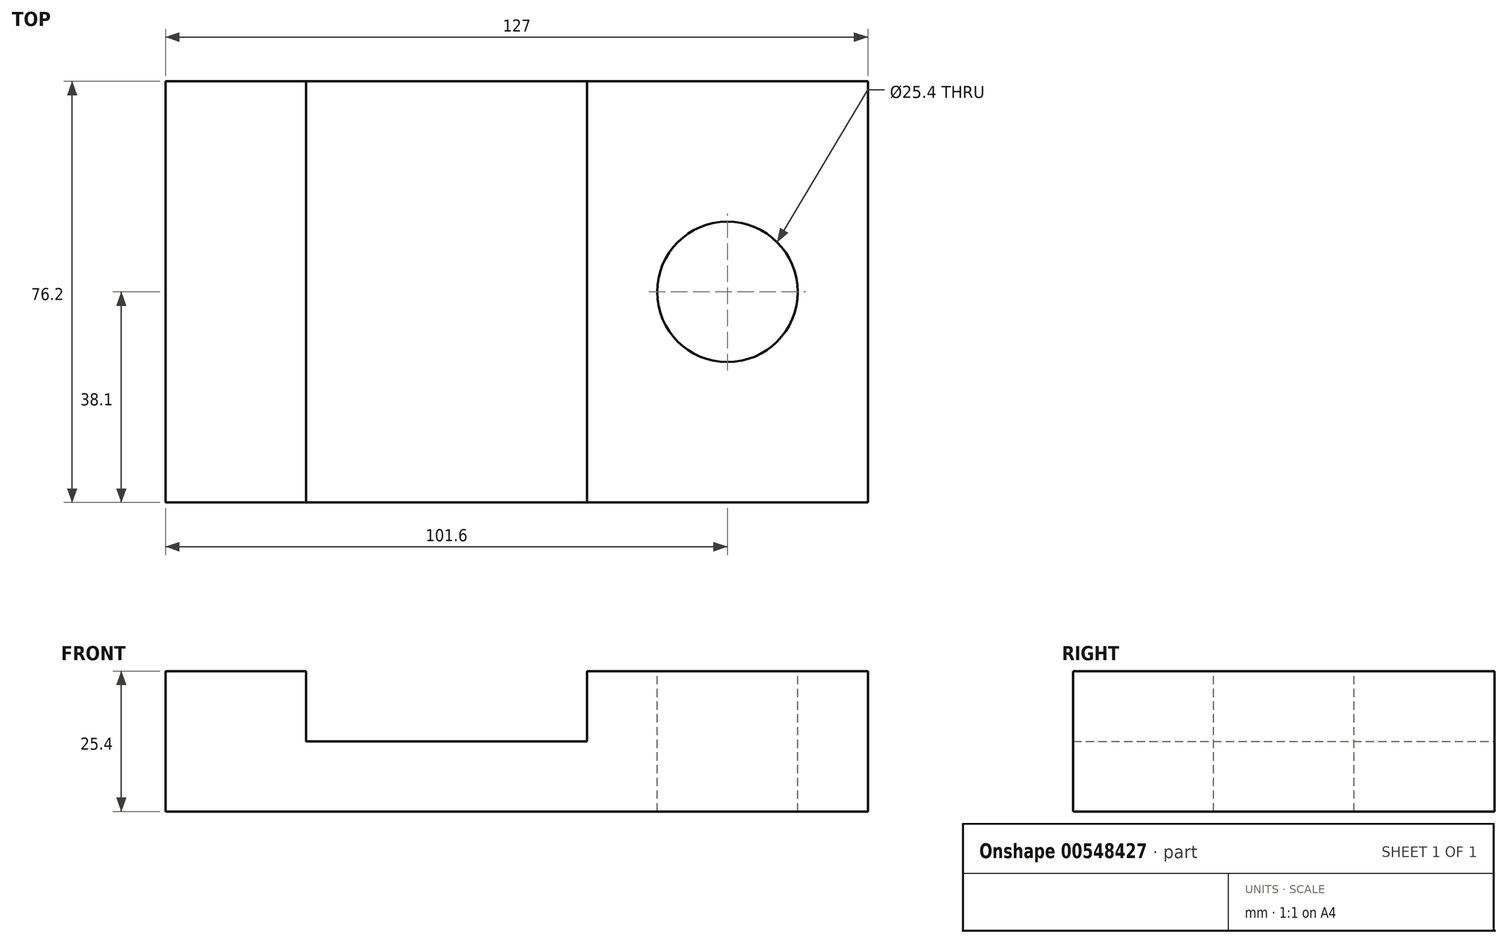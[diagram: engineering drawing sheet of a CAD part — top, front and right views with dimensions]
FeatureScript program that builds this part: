
annotation { "Feature Type Name" : "Feature", "Feature Type Description" : "" }
export const myFeature = defineFeature(function(context is Context, id is Id, definition is map)
    precondition{}
    {
        {
            var Q0;
            Q0=qCreatedBy(makeId("Front.planeOp"),FACE);
            var sketch = newSketch(context, id + "F0", { "sketchPlane" : qUnion([Q0])});
            skLineSegment(sketch, "E0.top", {"start": v(-63.5, -12.7) * mm, "end": v(63.5, -12.7) * mm});
            skLineSegment(sketch, "E0.left", {"start": v(-63.5, 12.7) * mm, "end": v(-63.5, -12.7) * mm});
            skLineSegment(sketch, "E0.right", {"start": v(63.5, 12.7) * mm, "end": v(63.5, -12.7) * mm});
            skPoint(sketch, "E0.middle", {"position": v(0, 0) * mm});
            skLineSegment(sketch, "E1", {"start": v(-63.5, 12.7) * mm, "end": v(-38.1, 12.7) * mm});
            skLineSegment(sketch, "E2", {"start": v(-38.1, 12.7) * mm, "end": v(-38.1, 0) * mm});
            skLineSegment(sketch, "E3", {"start": v(-38.1, 0) * mm, "end": v(12.7, 0) * mm});
            skLineSegment(sketch, "E4", {"start": v(12.7, 0) * mm, "end": v(12.7, 12.7) * mm});
            skLineSegment(sketch, "E5", {"start": v(12.7, 12.7) * mm, "end": v(63.5, 12.7) * mm});
            skSolve(sketch);
        }
        {
            var Q0;
            Q0 = qSketchRegion(id + "F0", true);
            extrude(context, id + "F1", {"entities" : qUnion([Q0]), "depth" : 76.2 * mm, "offsetDistance" : 25.4 * mm});
        }
        {
            var Q0;
            Q0=makeQuery(id+"F1.opExtrude","SWEPT_FACE",FACE,{"disambiguationData":[OSD([sQuery(id+"F0.wireOp",EDGE,"E5")])]});
            var sketch = newSketch(context, id + "F2", { "sketchPlane" : qUnion([Q0])});
            skCircle(sketch, "E6", {"center": v(38.1, -38.1) * mm, "radius": 12.7 * mm});
            skSolve(sketch);
        }
        {
            var Q0;
            Q0 = qSketchRegion(id + "F2", true);
            extrude(context, id + "F3", {"entities" : qUnion([Q0]), "operationType" : NewBodyOperationType.REMOVE, "oppositeDirection" : true, "depth" : 25.4 * mm, "offsetDistance" : 25.4 * mm});
        }
    });
